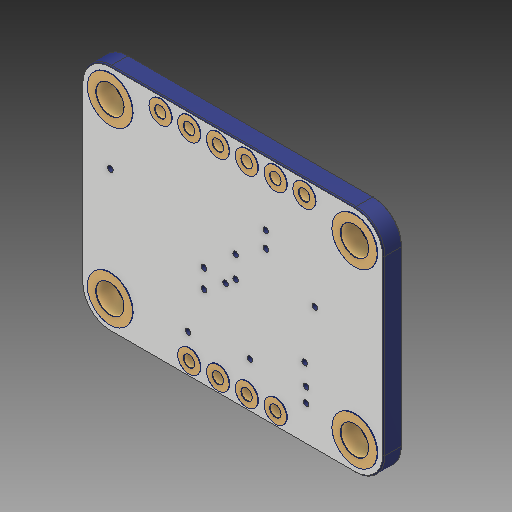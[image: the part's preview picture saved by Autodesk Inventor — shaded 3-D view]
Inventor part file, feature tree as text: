
AUTODESK INVENTOR PART (.ipt)
format: ipt  version: 2017.3 (Build 213257000, 257)  size: 846,336 bytes
history: native  units: mm
features: other x71, mirror x19, fillet x2, chamfer x2
ambient origin geometry x8: Origin, YZ Plane, XZ Plane, XY Plane, X Axis, Y Axis, Z Axis, Center Point
bodies: Volumenkörper1 (feature_tree), Volumenkörper2 (feature_tree), Volumenkörper3 (feature_tree), Volumenkörper4 (feature_tree), Volumenkörper5 (feature_tree), Volumenkörper6 (feature_tree), Volumenkörper7 (feature_tree), Volumenkörper8 (feature_tree), Volumenkörper9 (feature_tree), Volumenkörper10 (feature_tree), Volumenkörper11 (feature_tree), Volumenkörper12 (feature_tree), Volumenkörper13 (feature_tree), Volumenkörper14 (feature_tree), Volumenkörper15 (feature_tree), Volumenkörper16 (feature_tree), Volumenkörper17 (feature_tree), Volumenkörper18 (feature_tree), Volumenkörper19 (feature_tree), Volumenkörper20 (feature_tree), Volumenkörper21 (feature_tree), Volumenkörper22 (feature_tree), Volumenkörper23 (feature_tree), Volumenkörper24 (feature_tree), Volumenkörper25 (feature_tree), Volumenkörper26 (feature_tree), Volumenkörper27 (feature_tree), Volumenkörper28 (feature_tree), Volumenkörper29 (feature_tree), Volumenkörper30 (feature_tree), Volumenkörper31 (feature_tree), Volumenkörper32 (feature_tree), Volumenkörper33 (feature_tree), Volumenkörper34 (feature_tree), Volumenkörper35 (feature_tree), Volumenkörper36 (feature_tree), Volumenkörper37 (feature_tree), Volumenkörper38 (feature_tree), Volumenkörper39 (feature_tree), Volumenkörper40 (feature_tree), Volumenkörper41 (feature_tree), Volumenkörper42 (feature_tree), Volumenkörper43 (feature_tree), Volumenkörper44 (feature_tree), Volumenkörper45 (feature_tree), Volumenkörper46 (feature_tree), Volumenkörper47 (feature_tree), Volumenkörper48 (feature_tree), Volumenkörper49 (feature_tree), Volumenkörper50 (feature_tree), Volumenkörper51 (feature_tree), Volumenkörper52 (feature_tree), Volumenkörper53 (feature_tree), Volumenkörper54 (feature_tree), Volumenkörper55 (feature_tree), Volumenkörper56 (feature_tree), Volumenkörper57 (feature_tree), Volumenkörper58 (feature_tree), Volumenkörper59 (feature_tree), Volumenkörper60 (feature_tree), Volumenkörper61 (feature_tree), Volumenkörper62 (feature_tree), Volumenkörper63 (feature_tree), Volumenkörper64 (feature_tree), Volumenkörper65 (feature_tree), Volumenkörper66 (feature_tree), Volumenkörper67 (feature_tree), Volumenkörper68 (feature_tree), Volumenkörper69 (feature_tree), Volumenkörper70 (feature_tree), Volumenkörper71 (feature_tree), Volumenkörper72 (feature_tree), Volumenkörper73 (feature_tree), Volumenkörper74 (feature_tree), Volumenkörper75 (feature_tree), Volumenkörper76 (feature_tree), Volumenkörper77 (feature_tree), Volumenkörper78 (feature_tree), Volumenkörper79 (feature_tree), Volumenkörper80 (feature_tree), Volumenkörper81 (feature_tree), Volumenkörper82 (feature_tree), Volumenkörper83 (feature_tree), Volumenkörper84 (feature_tree), Volumenkörper85 (feature_tree), Volumenkörper86 (feature_tree), Volumenkörper87 (feature_tree), Volumenkörper88 (feature_tree), Volumenkörper89 (feature_tree), Volumenkörper90 (feature_tree), Volumenkörper91 (feature_tree), Volumenkörper92 (feature_tree), Volumenkörper93 (feature_tree), Volumenkörper94 (feature_tree)
feature tree (94):
  fillet  "Fillet2"  [1 undecoded]
  other  "Boss-Extrude4[1]"
  other  "Boss-Extrude4[2]"
  other  "Boss-Extrude4[3]"
  other  "Boss-Extrude4[4]"
  other  "Boss-Extrude4[5]"
  other  "Boss-Extrude4[6]"
  other  "Boss-Extrude5[1]"
  other  "Boss-Extrude5[2]"
  other  "Boss-Extrude5[3]"
  other  "Boss-Extrude5[4]"
  other  "Boss-Extrude5[5]"
  other  "Boss-Extrude5[6]"
  other  "Boss-Extrude5[7]"
  other  "Boss-Extrude5[8]"
  chamfer  "Chamfer4"  [1 undecoded]
  other  "Boss-Extrude7[1]"
  other  "Boss-Extrude7[2]"
  other  "LPattern3[1]"
  other  "LPattern3[2]"
  other  "LPattern4"
  chamfer  "Chamfer6"  [1 undecoded]
  other  "Boss-Extrude9"
  other  "LPattern5"
  other  "LPattern6"
  mirror  "Mirror1"
  mirror  "Mirror2[1]"
  mirror  "Mirror2[2]"
  mirror  "Mirror2[3]"
  mirror  "Mirror2[4]"
  other  "LPattern9[1]"
  other  "LPattern9[2]"
  other  "LPattern9[3]"
  other  "LPattern9[4]"
  other  "Boss-Extrude10[1]"
  other  "Boss-Extrude10[2]"
  other  "Boss-Extrude10[3]"
  other  "Boss-Extrude10[4]"
  other  "Boss-Extrude10[5]"
  other  "Boss-Extrude10[6]"
  other  "Boss-Extrude10[7]"
  other  "Boss-Extrude10[8]"
  other  "Boss-Extrude10[9]"
  other  "Boss-Extrude10[10]"
  other  "Boss-Extrude10[11]"
  other  "Boss-Extrude10[12]"
  other  "Boss-Extrude10[13]"
  other  "Boss-Extrude10[14]"
  other  "Boss-Extrude10[15]"
  other  "Boss-Extrude10[16]"
  mirror  "Mirror3[1]"
  mirror  "Mirror3[2]"
  mirror  "Mirror3[3]"
  mirror  "Mirror3[4]"
  mirror  "Mirror3[5]"
  mirror  "Mirror3[6]"
  mirror  "Mirror3[7]"
  mirror  "Mirror3[8]"
  mirror  "Mirror3[9]"
  mirror  "Mirror3[10]"
  mirror  "Mirror3[11]"
  mirror  "Mirror3[12]"
  mirror  "Mirror3[13]"
  mirror  "Mirror3[14]"
  fillet  "Fillet10"  [1 undecoded]
  other  "Boss-Extrude11[1]"
  other  "Boss-Extrude11[2]"
  other  "Boss-Extrude11[3]"
  other  "Boss-Extrude11[4]"
  other  "Boss-Extrude11[5]"
  other  "Boss-Extrude11[6]"
  other  "Boss-Extrude11[7]"
  other  "Boss-Extrude11[8]"
  other  "Boss-Extrude11[9]"
  other  "Boss-Extrude11[10]"
  other  "Boss-Extrude11[11]"
  other  "Boss-Extrude11[12]"
  other  "Boss-Extrude11[13]"
  other  "Boss-Extrude11[14]"
  other  "Boss-Extrude11[15]"
  other  "Boss-Extrude11[16]"
  other  "Boss-Extrude12[1]"
  other  "Boss-Extrude12[2]"
  other  "Boss-Extrude12[3]"
  other  "Boss-Extrude12[4]"
  other  "Boss-Extrude12[5]"
  other  "Boss-Extrude12[6]"
  other  "Boss-Extrude12[7]"
  other  "Boss-Extrude12[8]"
  other  "Boss-Extrude12[9]"
  other  "Boss-Extrude12[10]"
  other  "Boss-Extrude12[11]"
  other  "Boss-Extrude12[12]"
  other  "Boss-Extrude13"
note: 4 required parameter values undecoded (feature->parameter linkage not recoverable at this tier; creation-order binding heuristic only, values carry confidence <= 0.55)
